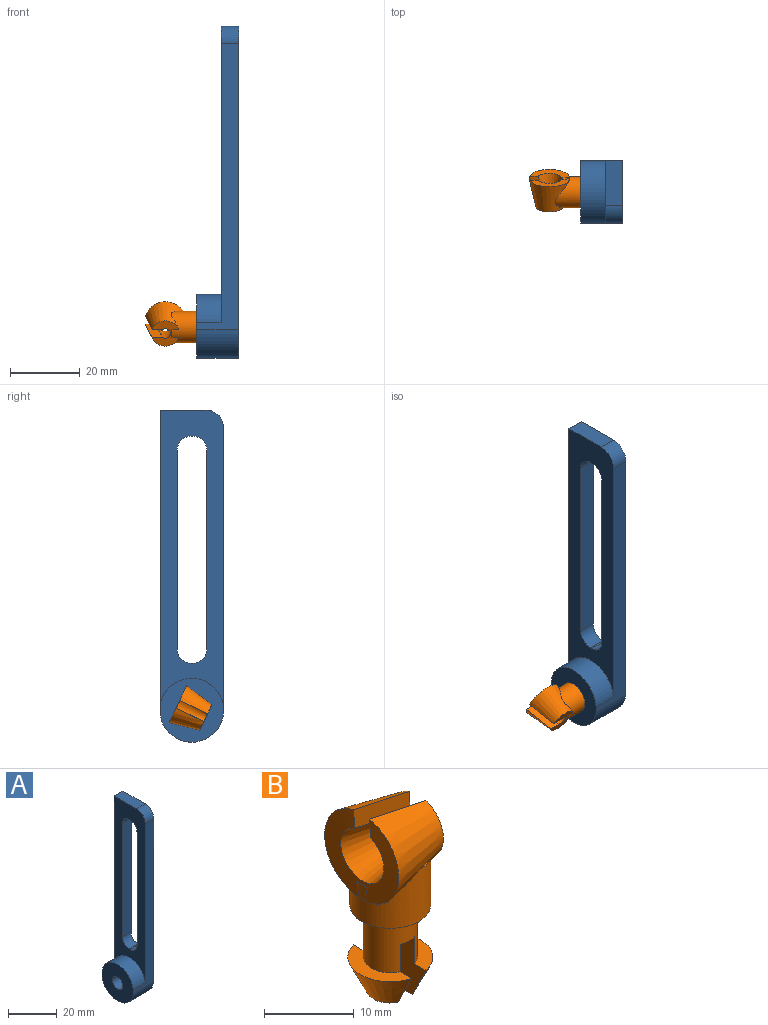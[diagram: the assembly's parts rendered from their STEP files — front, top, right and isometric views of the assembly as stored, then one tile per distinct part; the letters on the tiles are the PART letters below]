
ASSEMBLY  parts=2 mates=1
PART A: 24 faces, bbox 12x18x95 mm
  f0: plane 95x18mm, normal (1,0,0), area 1038.2mm2, adj f1,f2,f4,f5,f6,f7,f8,f9
  f1: cylinder r=8mm len=12mm, axis (-1,0,0), area 18.6mm2, adj f0,f4,f17,f19
  f2: plane 12x1.94mm, normal (0,0,-1), area 23.3mm2, adj f0,f18,f19,f20
  f3: plane 84.92x18mm, normal (-1,0,0), area 871.3mm2, adj f4,f5,f6,f7,f8,f9,f10,f11
  f4: plane 87x12mm, normal (0,1,0), area 457mm2, adj f0,f1,f3,f5,f16,f19
  f5: plane 13x5mm, normal (0,0,1), area 65mm2, adj f0,f3,f4,f11
  f6: plane 57x5mm, normal (0,-1,0), area 285mm2, adj f0,f3,f12,f13
  f7: plane 5x0.5mm, normal (0,0,1), area 2.5mm2, adj f0,f3,f13,f14
  f8: plane 57x5mm, normal (0,1,0), area 285mm2, adj f0,f3,f14,f15
  f9: plane 5x0.5mm, normal (0,0,-1), area 2.5mm2, adj f0,f3,f12,f15
  f10: plane 81.91x12mm, normal (0,-1,0), area 423.5mm2, adj f0,f3,f11,f16,f18,f19
  f11: cylinder r=5mm len=5mm, axis (-1,0,0), area 39.3mm2, adj f0,f3,f5,f10
  f12: cylinder r=4mm len=5mm, axis (-1,0,0), area 31.4mm2, adj f0,f3,f6,f9
  f13: cylinder r=4mm len=5mm, axis (1,0,0), area 31.4mm2, adj f0,f3,f6,f7
  f14: cylinder r=4mm len=5mm, axis (-1,0,0), area 31.4mm2, adj f0,f3,f7,f8
  f15: cylinder r=4mm len=5mm, axis (1,0,0), area 31.4mm2, adj f0,f3,f8,f9
  f16: cylinder r=9.14mm len=18mm, axis (-1,0,0), area 179.6mm2, adj f3,f4,f10,f19
  f17: cylinder r=9.14mm len=12mm, axis (-1,0,0), area 127.9mm2, adj f0,f1,f19,f20
  f18: cylinder r=9.14mm len=12mm, axis (-1,0,0), area 148mm2, adj f0,f2,f10,f19
  f19: plane 18.23x18mm, normal (-1,0,0), area 232.7mm2, adj f1,f2,f4,f10,f16,f17,f18,f20
  f20: cylinder r=8mm len=12mm, axis (-1,0,0), area 1.6mm2, adj f0,f2,f17,f19
  f21: cylinder r=3.05mm len=7mm, axis (1,0,0), area 134.1mm2, adj f19,f22
  f22: plane 11x11mm, normal (1,0,0), area 65.8mm2, adj f21,f23
  f23: cylinder r=5.5mm len=11mm, axis (1,0,0), area 172.8mm2, adj f0,f22
PART B: 23 faces, bbox 10.2x12.4x26.7 mm
  f0: cone r=5.83mm half-angle=11.7deg, axis (-1,0,0), area 95.3mm2, adj f2,f13,f15,f18,f21
  f1: plane 1.94x0.28mm, normal (0,0,1), area 0.1mm2, adj f2,f13
  f2: cylinder r=4.5mm len=9mm, axis (0,0,1), area 162.7mm2, adj f0,f1,f8,f13,f14,f15,f17,f18
  f3: cone r=0mm half-angle=25.3deg, axis (0,0,1), area 43.5mm2, adj f4,f5,f11
  f4: plane 9.15x3.53mm, normal (0,0,1), area 16.8mm2, adj f3,f7,f11
  f5: plane 4.77x1.47mm, normal (0,0,-1), area 5mm2, adj f3,f11
  f6: cone r=0mm half-angle=25.3deg, axis (0,0,1), area 45.7mm2, adj f9,f10,f22
  f7: cylinder r=3mm len=7.1mm, axis (0,0,1), area 117.1mm2, adj f4,f8,f9,f11,f12,f22
  f8: plane 9x9mm, normal (0,0,-1), area 35.3mm2, adj f2,f7
  f9: plane 9.25x3.73mm, normal (0,0,1), area 17.5mm2, adj f6,f7,f22
  f10: plane 4.95x1.67mm, normal (0,0,-1), area 6mm2, adj f6,f22
  f11: plane 9.38x8.3mm, normal (1,0,0), area 50.8mm2, adj f3,f4,f5,f7,f12
  f12: plane 6x2.2mm, normal (0,0,-1), area 12.9mm2, adj f7,f11,f22
  f13: cone r=3.39mm half-angle=87.6deg, axis (-1,0,0), area 61.8mm2, adj f0,f1,f2,f14,f16,f20,f21
  f14: cone r=5.83mm half-angle=11.7deg, axis (-1,0,0), area 95.3mm2, adj f2,f13,f15,f17,f20
  f15: plane 8x7.63mm, normal (1,0,0), area 31.8mm2, adj f0,f2,f14,f16,f19,f20,f21
  f16: cone r=1.5mm half-angle=12.2deg, axis (-1,0,0), area 109.3mm2, adj f13,f15,f20,f21
  f17: plane 1.68x0.38mm, normal (0,0,1), area 0.1mm2, adj f2,f14
  f18: plane 1.68x0.38mm, normal (0,0,1), area 0.1mm2, adj f0,f2
  f19: plane 2.32x0.15mm, normal (0,0,1), area 0.2mm2, adj f2,f15
  f20: plane 9.54x5.57mm, normal (0,1,0), area 23.5mm2, adj f13,f14,f15,f16
  f21: plane 9.54x5.57mm, normal (0,-1,0), area 23.5mm2, adj f0,f13,f15,f16
  f22: plane 9.43x8.25mm, normal (-1,0,0), area 52mm2, adj f6,f7,f9,f10,f12
PLACE A t=(-31.88,-23.56,7.12)mm
PLACE B rot(axis=(0.65,-0.41,-0.65),135.6deg) t=(-31.83,-23.56,-39.01)mm
MATE revolute B.f7 <-> A.f21  axis (-1,0,0) through (-35.38,-23.56,-39.01)mm
